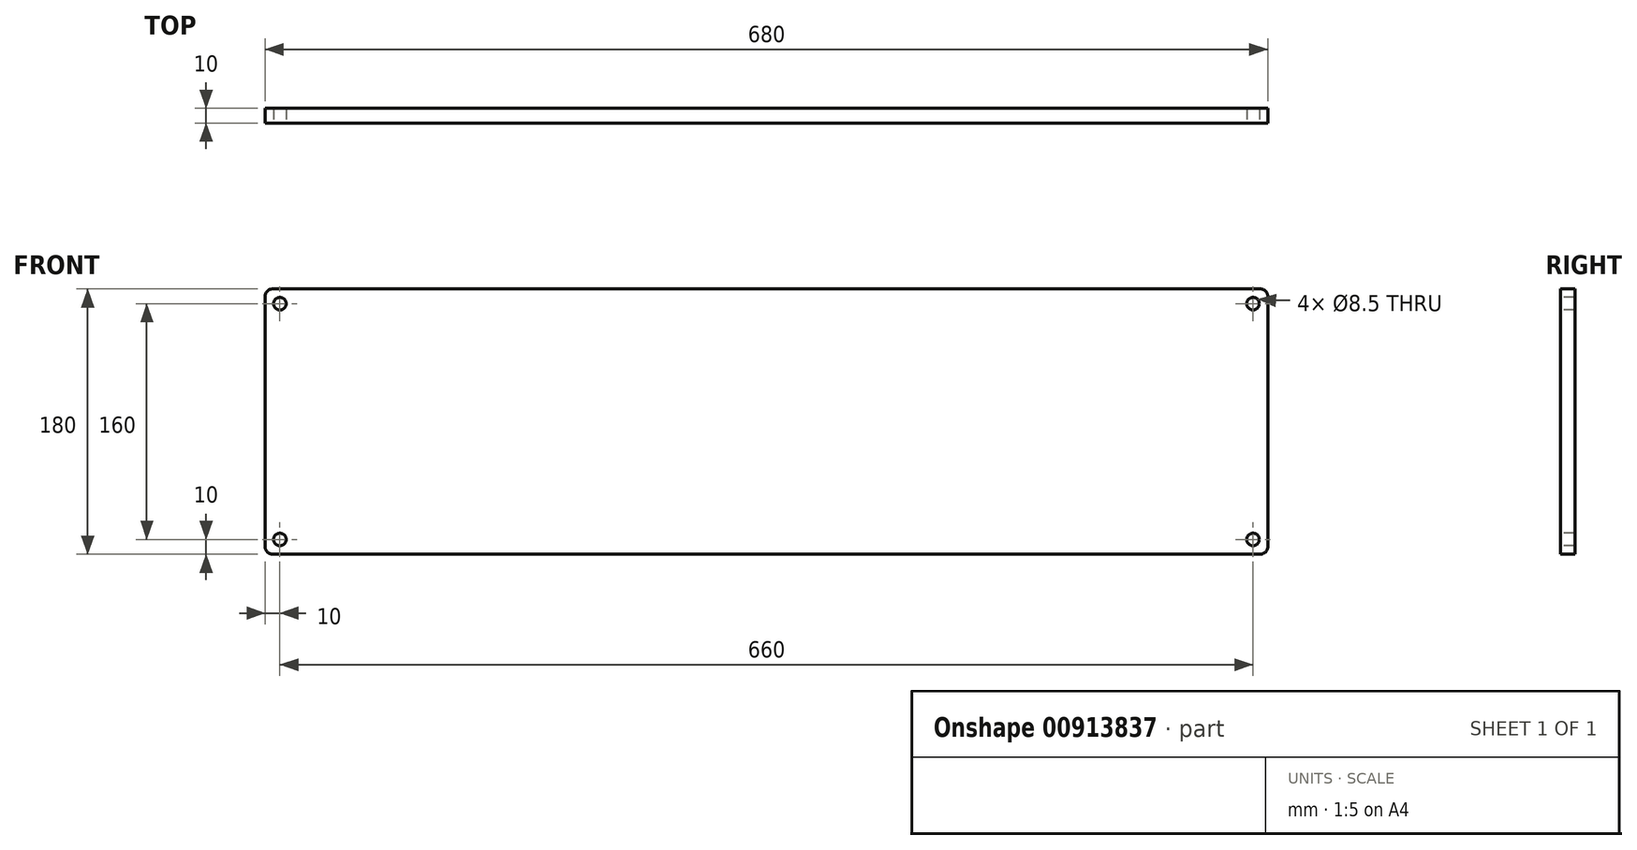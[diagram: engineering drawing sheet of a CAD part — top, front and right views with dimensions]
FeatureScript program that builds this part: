
annotation { "Feature Type Name" : "Feature", "Feature Type Description" : "" }
export const myFeature = defineFeature(function(context is Context, id is Id, definition is map)
    precondition{}
    {
        {
            var Q0;
            Q0=qCreatedBy(makeId("Front.planeOp"),FACE);
            var sketch = newSketch(context, id + "F0", { "sketchPlane" : qUnion([Q0])});
            skLineSegment(sketch, "E0.bottom", {"start": v(340, 90) * mm, "end": v(-340, 90) * mm});
            skLineSegment(sketch, "E0.top", {"start": v(340, -90) * mm, "end": v(-340, -90) * mm});
            skLineSegment(sketch, "E0.left", {"start": v(340, 90) * mm, "end": v(340, -90) * mm});
            skLineSegment(sketch, "E0.right", {"start": v(-340, 90) * mm, "end": v(-340, -90) * mm});
            skPoint(sketch, "E0.middle", {"position": v(0, 0) * mm});
            skSolve(sketch);
        }
        {
            var Q0;
            Q0=makeQuery(id+"F0.imprint","IMPRINT",FACE,{"disambiguationData":[TD([[makeQuery(id+"F0.imprint","IMPRINT",EDGE,{"derivedFrom":sQuery(id+"F0.wireOp",EDGE,"E0.bottom")}),1.0]])]});
            extrude(context, id + "F1", {"entities" : qUnion([Q0]), "depth" : 10 * mm, "offsetDistance" : 25 * mm});
        }
        {
            var Q0;
            Q0=makeQuery(id+"F1.opExtrude","SWEPT_EDGE",EDGE,{"disambiguationData":[OSD([sQuery(id+"F0.wireOp",EDGE,"E0.bottom"),sQuery(id+"F0.wireOp",EDGE,"E0.right")])]});
            var Q1;
            Q1=makeQuery(id+"F1.opExtrude","SWEPT_EDGE",EDGE,{"disambiguationData":[OSD([sQuery(id+"F0.wireOp",EDGE,"E0.bottom"),sQuery(id+"F0.wireOp",EDGE,"E0.left")])]});
            var Q2;
            Q2=makeQuery(id+"F1.opExtrude","SWEPT_EDGE",EDGE,{"disambiguationData":[OSD([sQuery(id+"F0.wireOp",EDGE,"E0.top"),sQuery(id+"F0.wireOp",EDGE,"E0.left")])]});
            var Q3;
            Q3=makeQuery(id+"F1.opExtrude","SWEPT_EDGE",EDGE,{"disambiguationData":[OSD([sQuery(id+"F0.wireOp",EDGE,"E0.top"),sQuery(id+"F0.wireOp",EDGE,"E0.right")])]});
            fillet(context, id + "F2", {"entities" : qUnion([Q0, Q1, Q2, Q3]), "radius" : 5 * mm, "tangentPropagation" : true, "allowEdgeOverflow" : false});
        }
        {
            var Q0;
            Q0=makeQuery(id+"F1.opExtrude","CAP_FACE",FACE,{"disambiguationData":[OSD([sQuery(id+"F0.wireOp",EDGE,"E0.bottom"),sQuery(id+"F0.wireOp",EDGE,"E0.top"),sQuery(id+"F0.wireOp",EDGE,"E0.left"),sQuery(id+"F0.wireOp",EDGE,"E0.right")])],"isStart":false});
            var sketch = newSketch(context, id + "F3", { "sketchPlane" : qUnion([Q0])});
            skLineSegment(sketch, "E1.bottom", {"start": v(-330, 80) * mm, "end": v(330, 80) * mm});
            skLineSegment(sketch, "E1.top", {"start": v(-330, -80) * mm, "end": v(330, -80) * mm});
            skLineSegment(sketch, "E1.left", {"start": v(-330, 80) * mm, "end": v(-330, -80) * mm});
            skLineSegment(sketch, "E1.right", {"start": v(330, 80) * mm, "end": v(330, -80) * mm});
            skPoint(sketch, "E1.middle", {"position": v(0, 0) * mm});
            skPoint(sketch, "E2", {"position": v(-330, 80) * mm});
            skPoint(sketch, "E3", {"position": v(-330, -80) * mm});
            skPoint(sketch, "E4", {"position": v(330, -80) * mm});
            skPoint(sketch, "E5", {"position": v(330, 80) * mm});
            skSolve(sketch);
        }
        {
            var Q0;
            Q0=sQuery(id+"F3.wireOp",VERTEX,"E2");
            var Q1;
            Q1=sQuery(id+"F3.wireOp",VERTEX,"E3");
            var Q2;
            Q2=sQuery(id+"F3.wireOp",VERTEX,"E1.top.end");
            var Q3;
            Q3=sQuery(id+"F3.wireOp",VERTEX,"E5");
            var Q4;
            Q4=makeQuery(id+"F1.opExtrude","SWEPT_BODY",BODY,{"disambiguationData":[OSD([sQuery(id+"F0.wireOp",EDGE,"E0.bottom"),sQuery(id+"F0.wireOp",EDGE,"E0.top"),sQuery(id+"F0.wireOp",EDGE,"E0.left"),sQuery(id+"F0.wireOp",EDGE,"E0.right")])]});
            hole(context, id + "F4", {"style" : HoleStyle.SIMPLE, "endStyle" : HoleEndStyle.THROUGH, "holeDiameter" : 8.5 * mm, "majorDiameter" : 5 * mm, "isTappedThrough" : true, "tappedDepth" : 12 * mm, "tapClearance" : 3, "locations" : qUnion([Q0, Q1, Q2, Q3]), "scope" : qUnion([Q4])});
        }
    });
